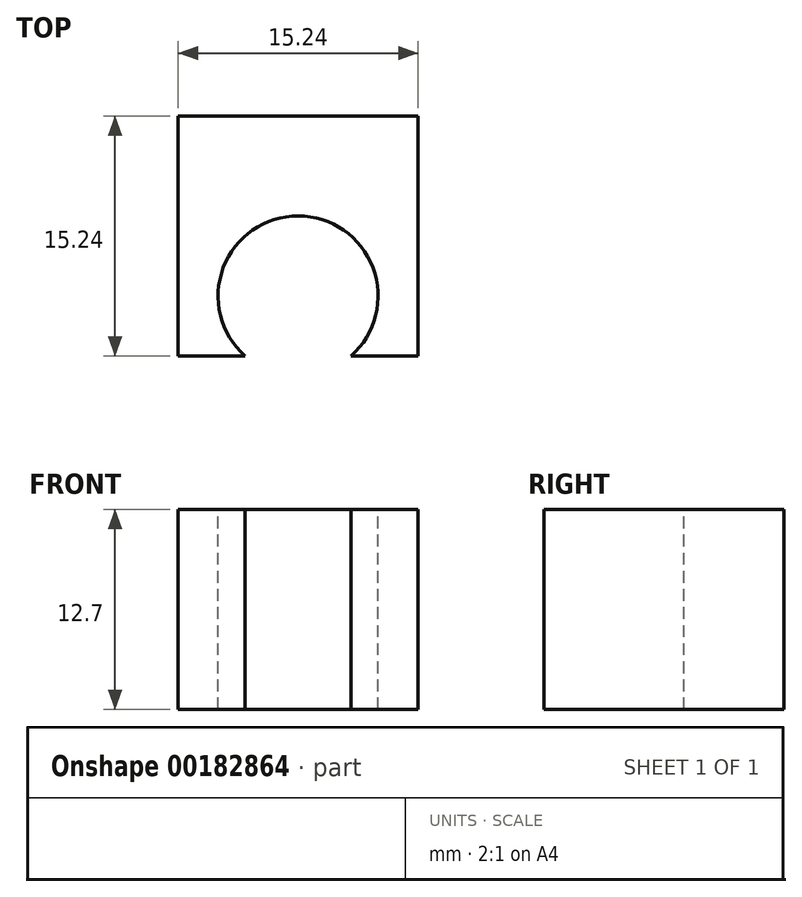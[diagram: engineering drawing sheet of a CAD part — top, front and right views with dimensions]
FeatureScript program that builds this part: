
annotation { "Feature Type Name" : "Feature", "Feature Type Description" : "" }
export const myFeature = defineFeature(function(context is Context, id is Id, definition is map)
    precondition{}
    {
        {
            var Q0;
            Q0=qCreatedBy(makeId("Top.planeOp"),FACE);
            var sketch = newSketch(context, id + "F0", { "sketchPlane" : qUnion([Q0])});
            skLineSegment(sketch, "E0.bottom", {"start": v(-10.58, -0.41) * mm, "end": v(4.66, -0.41) * mm});
            skLineSegment(sketch, "E0.top", {"start": v(-10.58, -15.65) * mm, "end": v(4.66, -15.65) * mm});
            skLineSegment(sketch, "E0.left", {"start": v(-10.58, -0.41) * mm, "end": v(-10.58, -15.65) * mm});
            skLineSegment(sketch, "E0.right", {"start": v(4.66, -0.41) * mm, "end": v(4.66, -15.65) * mm});
            skSolve(sketch);
        }
        {
            var Q0;
            Q0=makeQuery(id+"F0.imprint","IMPRINT",FACE,{"disambiguationData":[TD([[makeQuery(id+"F0.imprint","IMPRINT",EDGE,{"derivedFrom":sQuery(id+"F0.wireOp",EDGE,"E0.bottom")}),-1.0]])]});
            extrude(context, id + "F1", {"entities" : qUnion([Q0]), "depth" : 12.7 * mm});
        }
        {
            var Q0;
            Q0=makeQuery(id+"F1.opExtrude","CAP_FACE",FACE,{"disambiguationData":[OSD([sQuery(id+"F0.wireOp",EDGE,"E0.bottom"),sQuery(id+"F0.wireOp",EDGE,"E0.top"),sQuery(id+"F0.wireOp",EDGE,"E0.left"),sQuery(id+"F0.wireOp",EDGE,"E0.right")])],"isStart":false});
            var sketch = newSketch(context, id + "F2", { "sketchPlane" : qUnion([Q0])});
            skArc(sketch, "E1", {"start": v(0.4, -15.65) * mm, "mid": v(-2.96, -6.76) * mm, "end": v(-6.32, -15.65) * mm});
            skPoint(sketch, "E1.centerSnap0", {"position": v(-2.96, -15.65) * mm});
            skSolve(sketch);
        }
        {
            var Q0;
            {var subQ0=sQuery(id+"F2.wireOp",EDGE,"E1");Q0=makeQuery(id+"F2.imprint","IMPRINT",FACE,{"disambiguationData":[TD([[makeQuery(id+"F2.imprint","IMPRINT",EDGE,{"derivedFrom":subQ0}),1.0]])]});}
            extrude(context, id + "F3", {"entities" : qUnion([Q0]), "operationType" : NewBodyOperationType.REMOVE, "oppositeDirection" : true, "depth" : 12.7 * mm});
        }
    });
